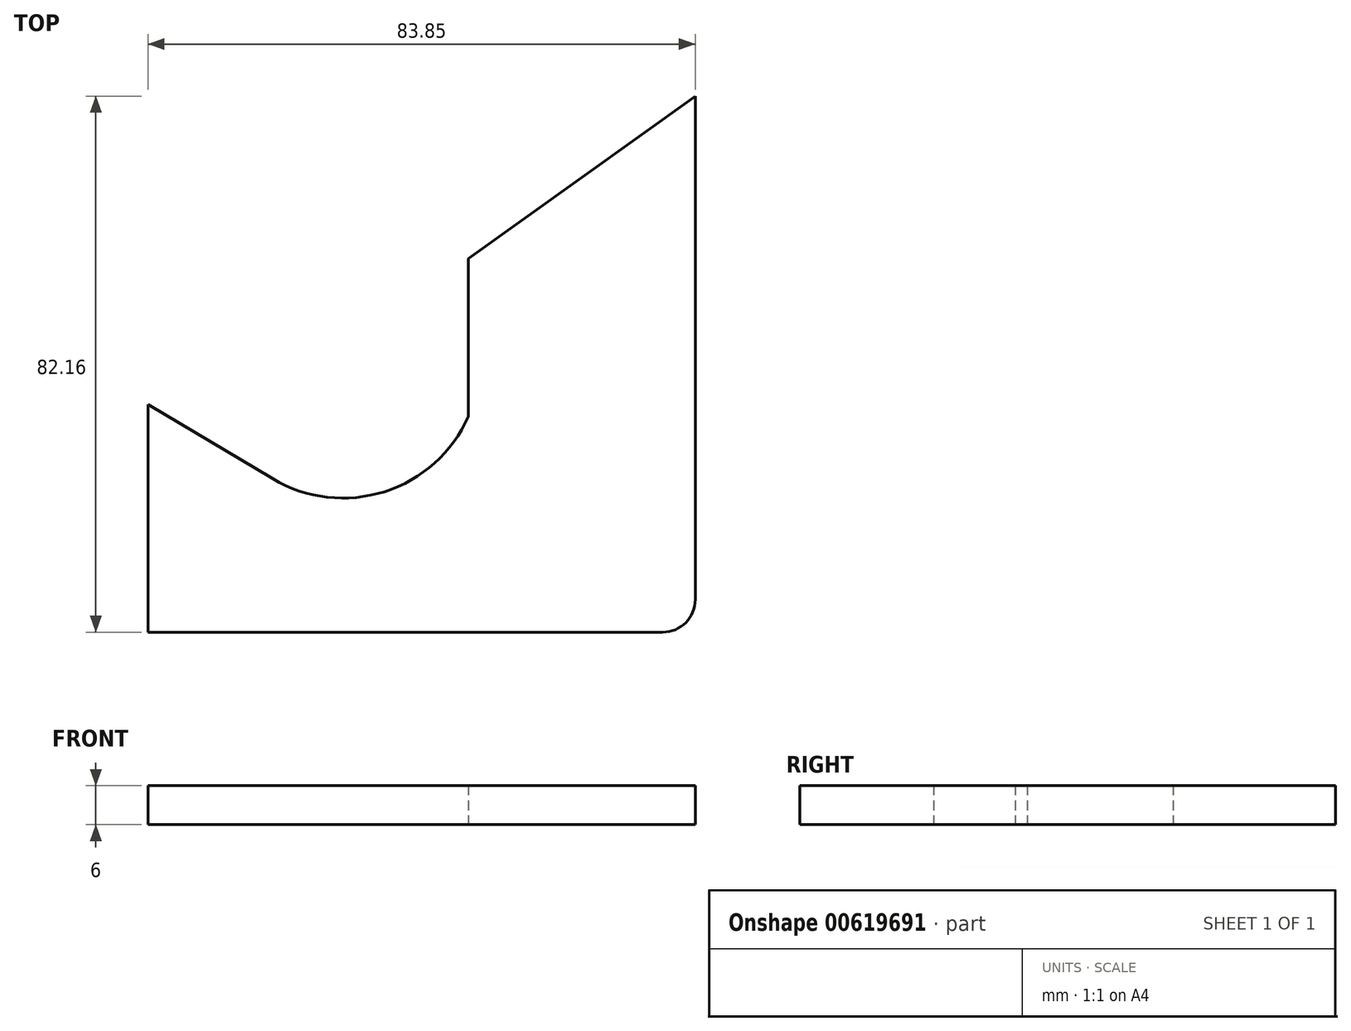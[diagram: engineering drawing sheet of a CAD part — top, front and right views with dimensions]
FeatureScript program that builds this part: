
annotation { "Feature Type Name" : "Feature", "Feature Type Description" : "" }
export const myFeature = defineFeature(function(context is Context, id is Id, definition is map)
    precondition{}
    {
        {
            var Q0;
            Q0=qCreatedBy(makeId("Top.planeOp"),FACE);
            var sketch = newSketch(context, id + "F0", { "sketchPlane" : qUnion([Q0])});
            skLineSegment(sketch, "E0", {"start": v(-34.2, -38.08) * mm, "end": v(49.66, -38.08) * mm});
            skLineSegment(sketch, "E1", {"start": v(49.66, -38.08) * mm, "end": v(49.66, 44.08) * mm});
            skLineSegment(sketch, "E2", {"start": v(49.66, 44.08) * mm, "end": v(14.9, 19.2) * mm});
            skLineSegment(sketch, "E3", {"start": v(14.9, 19.2) * mm, "end": v(14.9, -5.01) * mm});
            skArc(sketch, "E4", {"start": v(-15.1, -14.56) * mm, "mid": v(2.04, -16.54) * mm, "end": v(14.9, -5.01) * mm});
            skLineSegment(sketch, "E5", {"start": v(-15.1, -14.56) * mm, "end": v(-34.2, -3.18) * mm});
            skLineSegment(sketch, "E6", {"start": v(-34.2, -3.18) * mm, "end": v(-34.2, -38.08) * mm});
            skSolve(sketch);
        }
        {
            var Q0;
            Q0=makeQuery(id+"F0.imprint","IMPRINT",FACE,{"disambiguationData":[TD([[makeQuery(id+"F0.imprint","IMPRINT",EDGE,{"derivedFrom":sQuery(id+"F0.wireOp",EDGE,"E0")}),1.0]])]});
            extrude(context, id + "F1", {"entities" : qUnion([Q0]), "depth" : 6 * mm, "offsetDistance" : 25 * mm});
        }
        {
            var Q0;
            Q0=makeQuery(id+"F1.opExtrude","SWEPT_EDGE",EDGE,{"disambiguationData":[OSD([sQuery(id+"F0.wireOp",EDGE,"E0"),sQuery(id+"F0.wireOp",EDGE,"E1")])]});
            fillet(context, id + "F2", {"entities" : qUnion([Q0]), "radius" : 5 * mm, "tangentPropagation" : true, "allowEdgeOverflow" : false});
        }
    });
